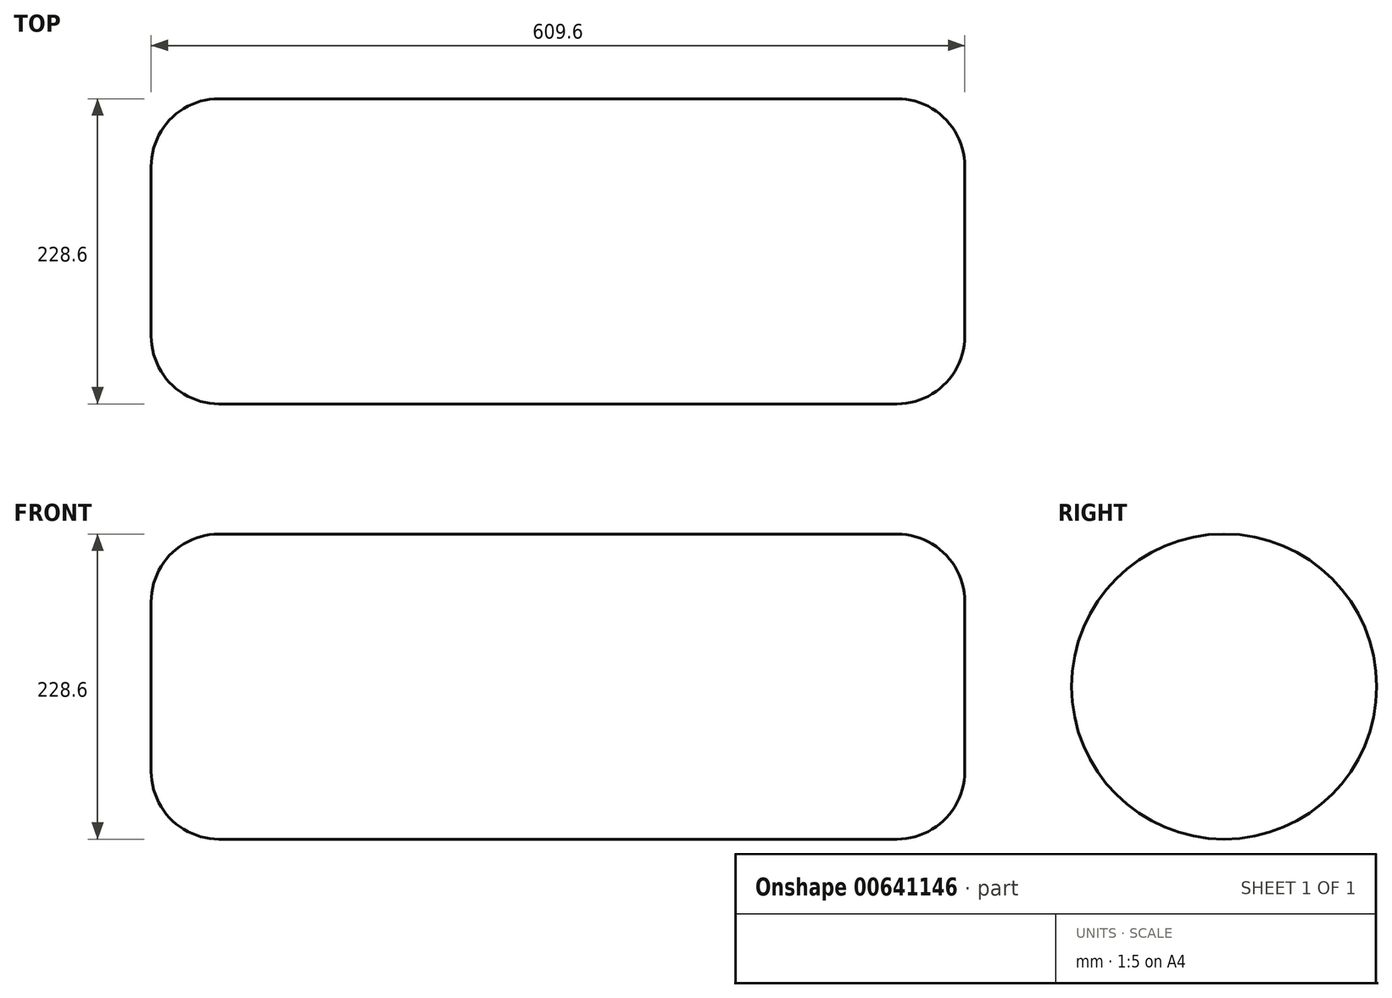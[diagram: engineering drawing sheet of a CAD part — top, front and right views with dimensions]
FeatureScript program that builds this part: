
annotation { "Feature Type Name" : "Feature", "Feature Type Description" : "" }
export const myFeature = defineFeature(function(context is Context, id is Id, definition is map)
    precondition{}
    {
        {
            var Q0;
            Q0=qCreatedBy(makeId("Right.planeOp"),FACE);
            var sketch = newSketch(context, id + "F0", { "sketchPlane" : qUnion([Q0])});
            skCircle(sketch, "E0", {"center": v(0, 0) * mm, "radius": 114.3 * mm});
            skSolve(sketch);
        }
        {
            var Q0;
            Q0=qSketchRegion(id+"F0",true);
            extrude(context, id + "F1", {"entities" : qUnion([Q0]), "depth" : 609.6 * mm});
        }
        {
            var Q0;
            Q0=makeQuery(id+"F1.opExtrude","CAP_EDGE",EDGE,{"disambiguationData":[OSD([sQuery(id+"F0.wireOp",EDGE,"E0")])],"isStart":true});
            var Q1;
            Q1=makeQuery(id+"F1.opExtrude","CAP_EDGE",EDGE,{"disambiguationData":[OSD([sQuery(id+"F0.wireOp",EDGE,"E0")])],"isStart":false});
            fillet(context, id + "F2", {"entities" : qUnion([Q0, Q1]), "radius" : 50.8 * mm, "tangentPropagation" : true, "allowEdgeOverflow" : false});
        }
    });
